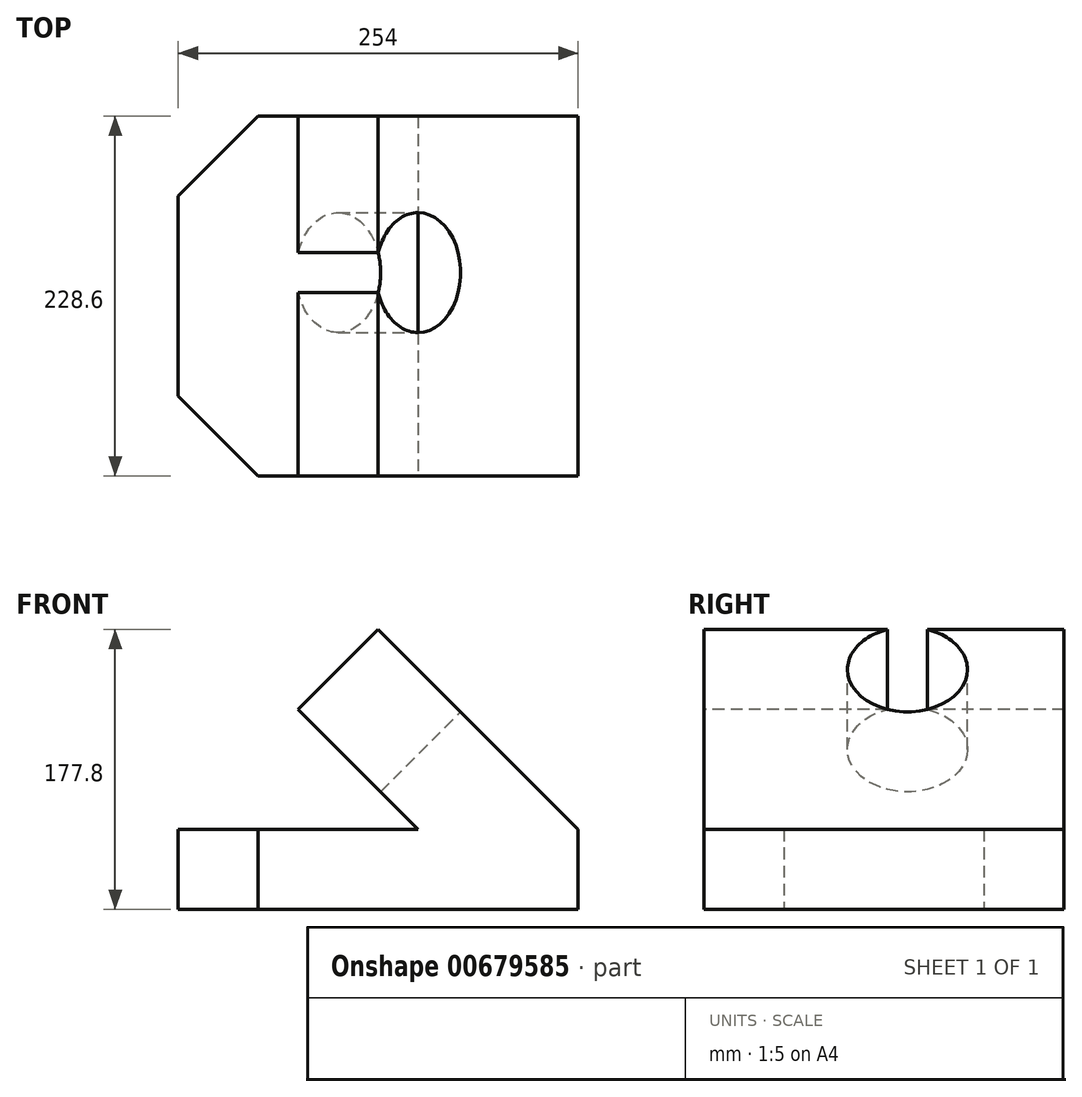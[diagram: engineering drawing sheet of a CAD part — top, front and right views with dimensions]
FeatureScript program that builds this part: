
annotation { "Feature Type Name" : "Feature", "Feature Type Description" : "" }
export const myFeature = defineFeature(function(context is Context, id is Id, definition is map)
    precondition{}
    {
        {
            var Q0;
            Q0=qCreatedBy(makeId("Front.planeOp"),FACE);
            var sketch = newSketch(context, id + "F0", { "sketchPlane" : qUnion([Q0])});
            skLineSegment(sketch, "E0", {"start": v(0, 0) * mm, "end": v(254, 0) * mm});
            skLineSegment(sketch, "E1", {"start": v(254, 0) * mm, "end": v(254, 50.8) * mm});
            skLineSegment(sketch, "E2", {"start": v(0, 0) * mm, "end": v(0, 50.8) * mm});
            skLineSegment(sketch, "E3", {"start": v(0, 50.8) * mm, "end": v(152.4, 50.8) * mm});
            skLineSegment(sketch, "E4", {"start": v(152.4, 50.8) * mm, "end": v(152.4, 127) * mm, "construction": true});
            skLineSegment(sketch, "E5", {"start": v(152.4, 127) * mm, "end": v(76.2, 127) * mm, "construction": true});
            skLineSegment(sketch, "E6", {"start": v(76.2, 127) * mm, "end": v(152.4, 50.8) * mm});
            skLineSegment(sketch, "E7", {"start": v(76.2, 127) * mm, "end": v(76.2, 177.8) * mm, "construction": true});
            skLineSegment(sketch, "E8", {"start": v(76.2, 177.8) * mm, "end": v(127, 177.8) * mm, "construction": true});
            skLineSegment(sketch, "E9", {"start": v(127, 177.8) * mm, "end": v(76.2, 127) * mm});
            skLineSegment(sketch, "E10", {"start": v(127, 177.8) * mm, "end": v(254, 50.8) * mm});
            skLineSegment(sketch, "E11", {"start": v(0, 50.8) * mm, "end": v(50.8, 50.8) * mm});
            skLineSegment(sketch, "E12", {"start": v(50.8, 50.8) * mm, "end": v(50.8, 0) * mm});
            skSolve(sketch);
        }
        {
            var Q0;
            {var subQ0=sQuery(id+"F0.wireOp",EDGE,"E1");Q0=makeQuery(id+"F0.imprint","IMPRINT",FACE,{"disambiguationData":[TD([[makeQuery(id+"F0.imprint","IMPRINT",EDGE,{"derivedFrom":subQ0}),1.0]])]});}
            var Q1;
            Q1=makeQuery(id+"F0.imprint","IMPRINT",FACE,{"disambiguationData":[TD([[makeQuery(id+"F0.imprint","IMPRINT",EDGE,{"derivedFrom":sQuery(id+"F0.wireOp",EDGE,"E4")}),1.0]])]});
            extrude(context, id + "F1", {"entities" : qUnion([Q0, Q1]), "endBound" : BoundingType.SYMMETRIC, "oppositeDirection" : true, "depth" : 228.6 * mm, "offsetDistance" : 25.4 * mm});
        }
        {
            var Q0;
            Q0=makeQuery(id+"F1.opExtrude","SWEPT_FACE",FACE,{"disambiguationData":[OSD([sQuery(id+"F0.wireOp",EDGE,"E0")])]});
            var sketch = newSketch(context, id + "F2", { "sketchPlane" : qUnion([Q0])});
            skLineSegment(sketch, "E13", {"start": v(50.8, 114.3) * mm, "end": v(0, 114.3) * mm});
            skLineSegment(sketch, "E14", {"start": v(0, 114.3) * mm, "end": v(0, 63.5) * mm});
            skLineSegment(sketch, "E15", {"start": v(0, 63.5) * mm, "end": v(0, 0) * mm});
            skLineSegment(sketch, "E16", {"start": v(0, 0) * mm, "end": v(0, -63.5) * mm});
            skLineSegment(sketch, "E17", {"start": v(0, -63.5) * mm, "end": v(0, -114.3) * mm});
            skLineSegment(sketch, "E18", {"start": v(0, -114.3) * mm, "end": v(50.8, -114.3) * mm});
            skLineSegment(sketch, "E19", {"start": v(50.8, -114.3) * mm, "end": v(0, -63.5) * mm});
            skLineSegment(sketch, "E20", {"start": v(0, 63.5) * mm, "end": v(50.8, 114.3) * mm});
            skSolve(sketch);
        }
        {
            var Q0;
            Q0=makeQuery(id+"F2.imprint","IMPRINT",FACE,{"disambiguationData":[TD([[makeQuery(id+"F2.imprint","IMPRINT",EDGE,{"derivedFrom":sQuery(id+"F2.wireOp",EDGE,"E15")}),1.0]])]});
            extrude(context, id + "F3", {"entities" : qUnion([Q0]), "operationType" : NewBodyOperationType.ADD, "oppositeDirection" : true, "depth" : 50.8 * mm, "offsetDistance" : 25.4 * mm});
        }
        {
            var Q0;
            Q0=makeQuery(id+"F1.opExtrude","SWEPT_FACE",FACE,{"disambiguationData":[OSD([sQuery(id+"F0.wireOp",EDGE,"E10")])]});
            var sketch = newSketch(context, id + "F4", { "sketchPlane" : qUnion([Q0])});
            skLineSegment(sketch, "E21", {"start": v(-35.92, -114.3) * mm, "end": v(-35.92, 0) * mm});
            skLineSegment(sketch, "E22", {"start": v(-35.92, 0) * mm, "end": v(-35.92, 114.3) * mm});
            skLineSegment(sketch, "E23", {"start": v(-35.92, 0) * mm, "end": v(14.88, 0) * mm});
            skCircle(sketch, "E24", {"center": v(14.88, 0) * mm, "radius": 38.1 * mm});
            skSolve(sketch);
        }
        {
            var Q0;
            Q0=makeQuery(id+"F4.imprint","IMPRINT",FACE,{"disambiguationData":[TD([[makeQuery(id+"F4.imprint","IMPRINT",EDGE,{"derivedFrom":sQuery(id+"F4.wireOp",EDGE,"E24")}),1.0]])]});
            extrude(context, id + "F5", {"entities" : qUnion([Q0]), "operationType" : NewBodyOperationType.REMOVE, "endBound" : BoundingType.SYMMETRIC, "oppositeDirection" : true, "depth" : 152.4 * mm, "offsetDistance" : 25.4 * mm});
        }
    });
